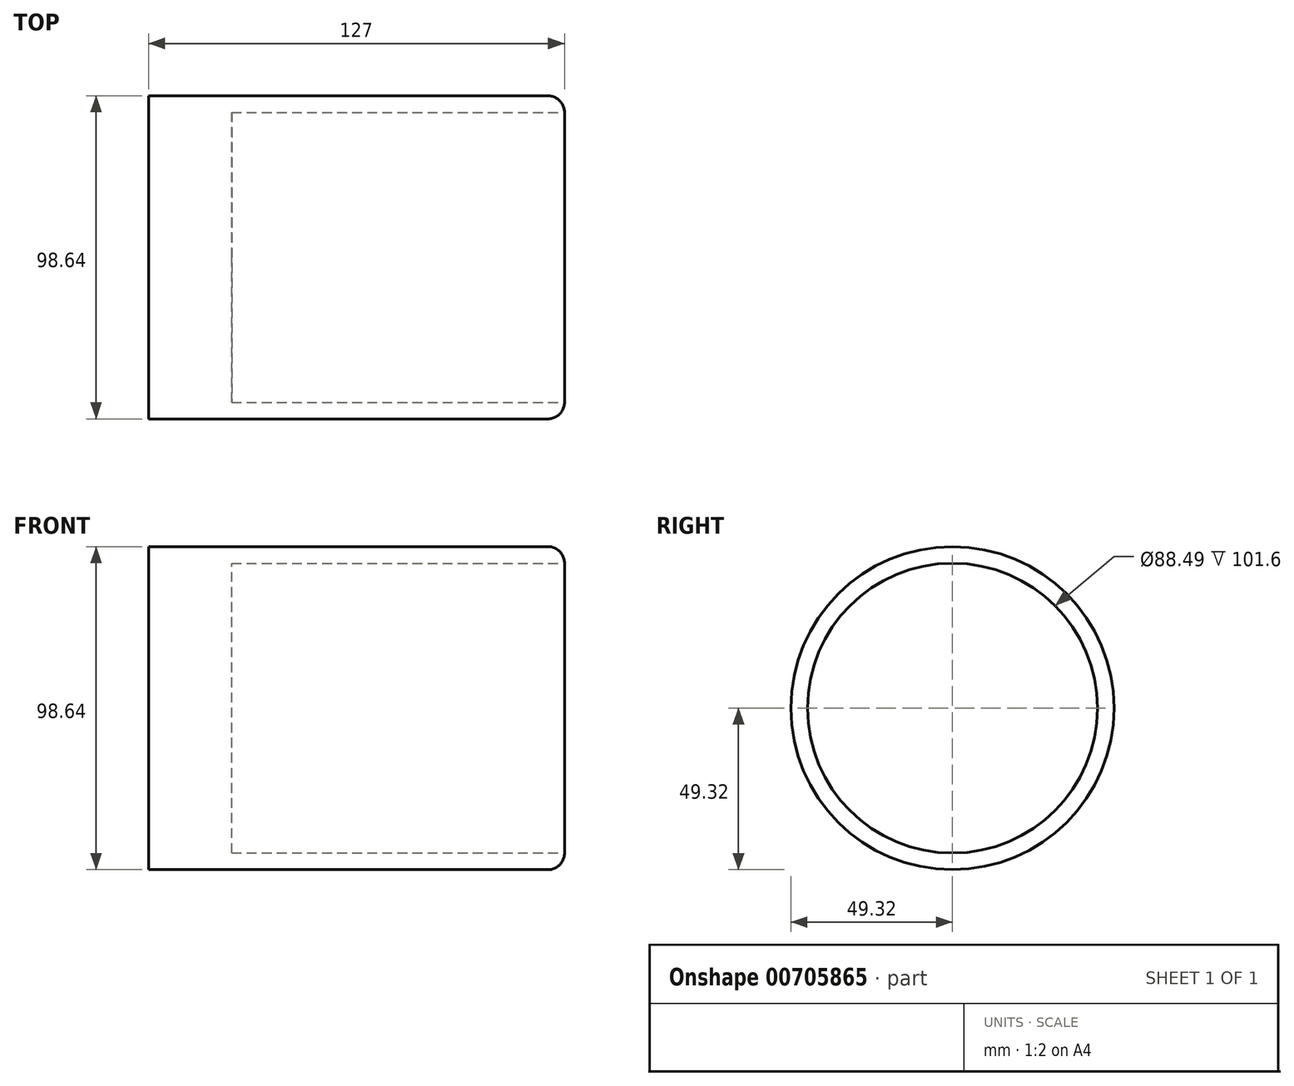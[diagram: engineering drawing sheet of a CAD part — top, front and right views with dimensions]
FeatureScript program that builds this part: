
annotation { "Feature Type Name" : "Feature", "Feature Type Description" : "" }
export const myFeature = defineFeature(function(context is Context, id is Id, definition is map)
    precondition{}
    {
        {
            var Q0;
            Q0=qCreatedBy(makeId("Right.planeOp"),FACE);
            var sketch = newSketch(context, id + "F0", { "sketchPlane" : qUnion([Q0])});
            skCircle(sketch, "E0", {"center": v(0, 0) * mm, "radius": 49.32 * mm});
            skSolve(sketch);
        }
        {
            var Q0;
            Q0 = qSketchRegion(id + "F0", true);
            extrude(context, id + "F1", {"entities" : qUnion([Q0]), "depth" : 127 * mm, "offsetDistance" : 25.4 * mm});
        }
        {
            var Q0;
            Q0=makeQuery(id+"F1.opExtrude","CAP_FACE",FACE,{"disambiguationData":[OSD([sQuery(id+"F0.wireOp",EDGE,"E0")])],"isStart":false});
            fillet(context, id + "F2", {"entities" : qUnion([Q0]), "radius" : 5.08 * mm, "tangentPropagation" : true, "allowEdgeOverflow" : false});
        }
        {
            var Q0;
            Q0=makeQuery(id+"F1.opExtrude","CAP_FACE",FACE,{"disambiguationData":[OSD([sQuery(id+"F0.wireOp",EDGE,"E0")])],"isStart":false});
            extrude(context, id + "F3", {"entities" : qUnion([Q0]), "operationType" : NewBodyOperationType.REMOVE, "oppositeDirection" : true, "depth" : 25.4 * mm, "offsetDistance" : 25.4 * mm});
        }
        {
            var Q0;
            Q0=makeQuery(id+"F3.boolean.opBoolean","COPY",FACE,{"derivedFrom":makeQuery(id+"F3.opExtrude","CAP_FACE",FACE,{"disambiguationData":[OSD([sQuery(id+"F0.wireOp",EDGE,"E0")])],"isStart":false})});
            extrude(context, id + "F4", {"entities" : qUnion([Q0]), "operationType" : NewBodyOperationType.REMOVE, "oppositeDirection" : true, "depth" : 25.4 * mm, "offsetDistance" : 25.4 * mm});
        }
        {
            var Q0;
            Q0=makeQuery(id+"F4.boolean.opBoolean","COPY",FACE,{"derivedFrom":makeQuery(id+"F4.opExtrude","CAP_FACE",FACE,{"disambiguationData":[OSD([sQuery(id+"F0.wireOp",EDGE,"E0")])],"isStart":false})});
            extrude(context, id + "F5", {"entities" : qUnion([Q0]), "operationType" : NewBodyOperationType.REMOVE, "oppositeDirection" : true, "depth" : 25.4 * mm, "offsetDistance" : 25.4 * mm});
        }
        {
            var Q0;
            Q0=makeQuery(id+"F5.boolean.opBoolean","COPY",FACE,{"derivedFrom":makeQuery(id+"F5.opExtrude","CAP_FACE",FACE,{"disambiguationData":[OSD([sQuery(id+"F0.wireOp",EDGE,"E0")])],"isStart":false})});
            extrude(context, id + "F6", {"entities" : qUnion([Q0]), "operationType" : NewBodyOperationType.REMOVE, "oppositeDirection" : true, "depth" : 25.4 * mm, "offsetDistance" : 25.4 * mm});
        }
    });
